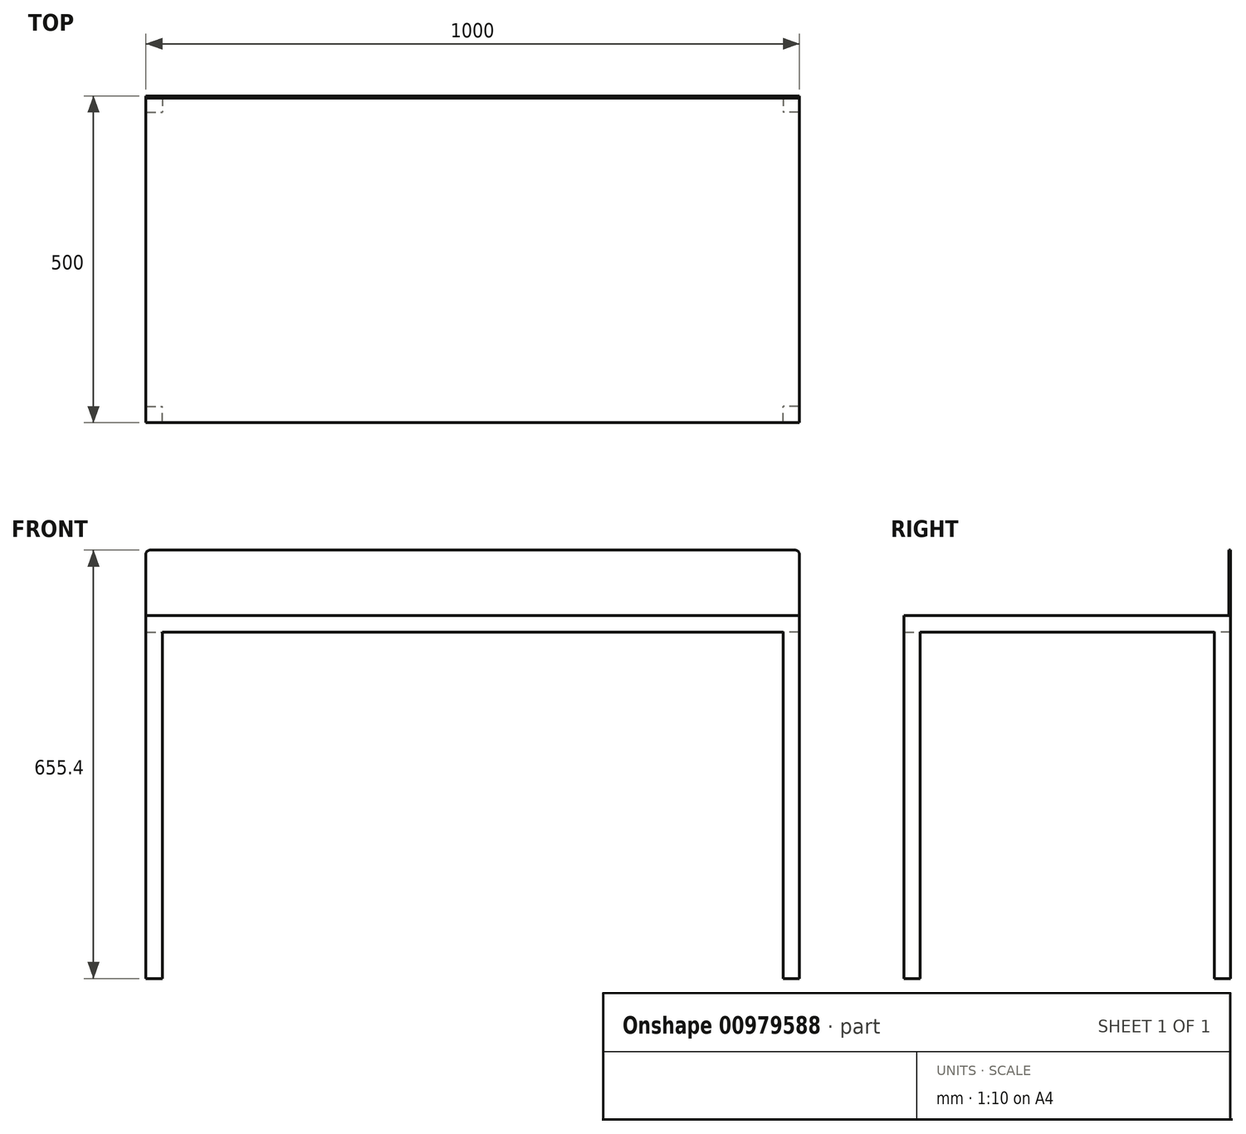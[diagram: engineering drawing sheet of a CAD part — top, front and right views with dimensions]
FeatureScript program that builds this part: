
annotation { "Feature Type Name" : "Feature", "Feature Type Description" : "" }
export const myFeature = defineFeature(function(context is Context, id is Id, definition is map)
    precondition{}
    {
        {
            var Q0;
            Q0=qCreatedBy(makeId("Top.planeOp"),FACE);
            var sketch = newSketch(context, id + "F0", { "sketchPlane" : qUnion([Q0])});
            skLineSegment(sketch, "E0.bottom", {"start": v(500, -250) * mm, "end": v(-500, -250) * mm});
            skLineSegment(sketch, "E0.top", {"start": v(500, 250) * mm, "end": v(-500, 250) * mm});
            skLineSegment(sketch, "E0.left", {"start": v(500, -250) * mm, "end": v(500, 250) * mm});
            skLineSegment(sketch, "E0.right", {"start": v(-500, -250) * mm, "end": v(-500, 250) * mm});
            skPoint(sketch, "E0.middle", {"position": v(0, 0) * mm});
            skSolve(sketch);
        }
        {
            var Q0;
            Q0 = qSketchRegion(id + "F0", true);
            extrude(context, id + "F1", {"entities" : qUnion([Q0]), "depth" : 25.4 * mm, "offsetDistance" : 25.4 * mm});
        }
        {
            var Q0;
            Q0=makeQuery(id+"F1.opExtrude","CAP_FACE",FACE,{"disambiguationData":[OSD([sQuery(id+"F0.wireOp",EDGE,"E0.bottom"),sQuery(id+"F0.wireOp",EDGE,"E0.top"),sQuery(id+"F0.wireOp",EDGE,"E0.left"),sQuery(id+"F0.wireOp",EDGE,"E0.right")])],"isStart":true});
            var sketch = newSketch(context, id + "F2", { "sketchPlane" : qUnion([Q0])});
            skLineSegment(sketch, "E1.bottom", {"start": v(-500, 250) * mm, "end": v(-475, 250) * mm});
            skLineSegment(sketch, "E1.top", {"start": v(-500, 225) * mm, "end": v(-475, 225) * mm});
            skLineSegment(sketch, "E1.left", {"start": v(-500, 250) * mm, "end": v(-500, 225) * mm});
            skLineSegment(sketch, "E1.right", {"start": v(-475, 250) * mm, "end": v(-475, 225) * mm});
            skLineSegment(sketch, "E2.bottom", {"start": v(-500, -250) * mm, "end": v(-475, -250) * mm});
            skLineSegment(sketch, "E2.top", {"start": v(-500, -225) * mm, "end": v(-475, -225) * mm});
            skLineSegment(sketch, "E2.left", {"start": v(-500, -250) * mm, "end": v(-500, -225) * mm});
            skLineSegment(sketch, "E2.right", {"start": v(-475, -250) * mm, "end": v(-475, -225) * mm});
            skLineSegment(sketch, "E3.bottom", {"start": v(500, 250) * mm, "end": v(475, 250) * mm});
            skLineSegment(sketch, "E3.top", {"start": v(500, 225) * mm, "end": v(475, 225) * mm});
            skLineSegment(sketch, "E3.left", {"start": v(500, 250) * mm, "end": v(500, 225) * mm});
            skLineSegment(sketch, "E3.right", {"start": v(475, 250) * mm, "end": v(475, 225) * mm});
            skLineSegment(sketch, "E4.bottom", {"start": v(500, -250) * mm, "end": v(475, -250) * mm});
            skLineSegment(sketch, "E4.top", {"start": v(500, -225) * mm, "end": v(475, -225) * mm});
            skLineSegment(sketch, "E4.left", {"start": v(500, -250) * mm, "end": v(500, -225) * mm});
            skLineSegment(sketch, "E4.right", {"start": v(475, -250) * mm, "end": v(475, -225) * mm});
            skSolve(sketch);
        }
        {
            var Q0;
            Q0 = qSketchRegion(id + "F2", true);
            extrude(context, id + "F3", {"entities" : qUnion([Q0]), "operationType" : NewBodyOperationType.ADD, "depth" : 530 * mm, "offsetDistance" : 25.4 * mm});
        }
        {
            var Q0;
            Q0=makeQuery(id+"F3.boolean.opBoolean","MERGE",FACE,{"derivedFrom":[makeQuery(id+"F1.opExtrude","SWEPT_FACE",FACE,{"disambiguationData":[OSD([sQuery(id+"F0.wireOp",EDGE,"E0.top")])]}),makeQuery(id+"F3.opExtrude","SWEPT_FACE",FACE,{"disambiguationData":[OSD([sQuery(id+"F2.wireOp",EDGE,"E2.bottom")])]}),makeQuery(id+"F3.opExtrude","SWEPT_FACE",FACE,{"disambiguationData":[OSD([sQuery(id+"F2.wireOp",EDGE,"E4.bottom")])]})]});
            var sketch = newSketch(context, id + "F4", { "sketchPlane" : qUnion([Q0])});
            skLineSegment(sketch, "E5", {"start": v(-500, 25.4) * mm, "end": v(-500, 119.05) * mm});
            skLineSegment(sketch, "E6", {"start": v(-493.65, 125.4) * mm, "end": v(493.65, 125.4) * mm});
            skLineSegment(sketch, "E7", {"start": v(500, 119.05) * mm, "end": v(500, 25.4) * mm});
            skLineSegment(sketch, "E8", {"start": v(500, 25.4) * mm, "end": v(-500, 25.4) * mm});
            skPoint(sketch, "E9.visualSharp", {"position": v(500, 125.4) * mm});
            skArc(sketch, "E9.filletArc", {"start": v(500, 119.05) * mm, "mid": v(498.14, 123.54) * mm, "end": v(493.65, 125.4) * mm});
            skPoint(sketch, "E10.visualSharp", {"position": v(-500, 125.4) * mm});
            skArc(sketch, "E10.filletArc", {"start": v(-493.65, 125.4) * mm, "mid": v(-498.14, 123.54) * mm, "end": v(-500, 119.05) * mm});
            skSolve(sketch);
        }
        {
            var Q0;
            Q0 = qSketchRegion(id + "F4", true);
            extrude(context, id + "F5", {"entities" : qUnion([Q0]), "operationType" : NewBodyOperationType.ADD, "oppositeDirection" : true, "depth" : 3 * mm, "offsetDistance" : 25.4 * mm});
        }
    });
